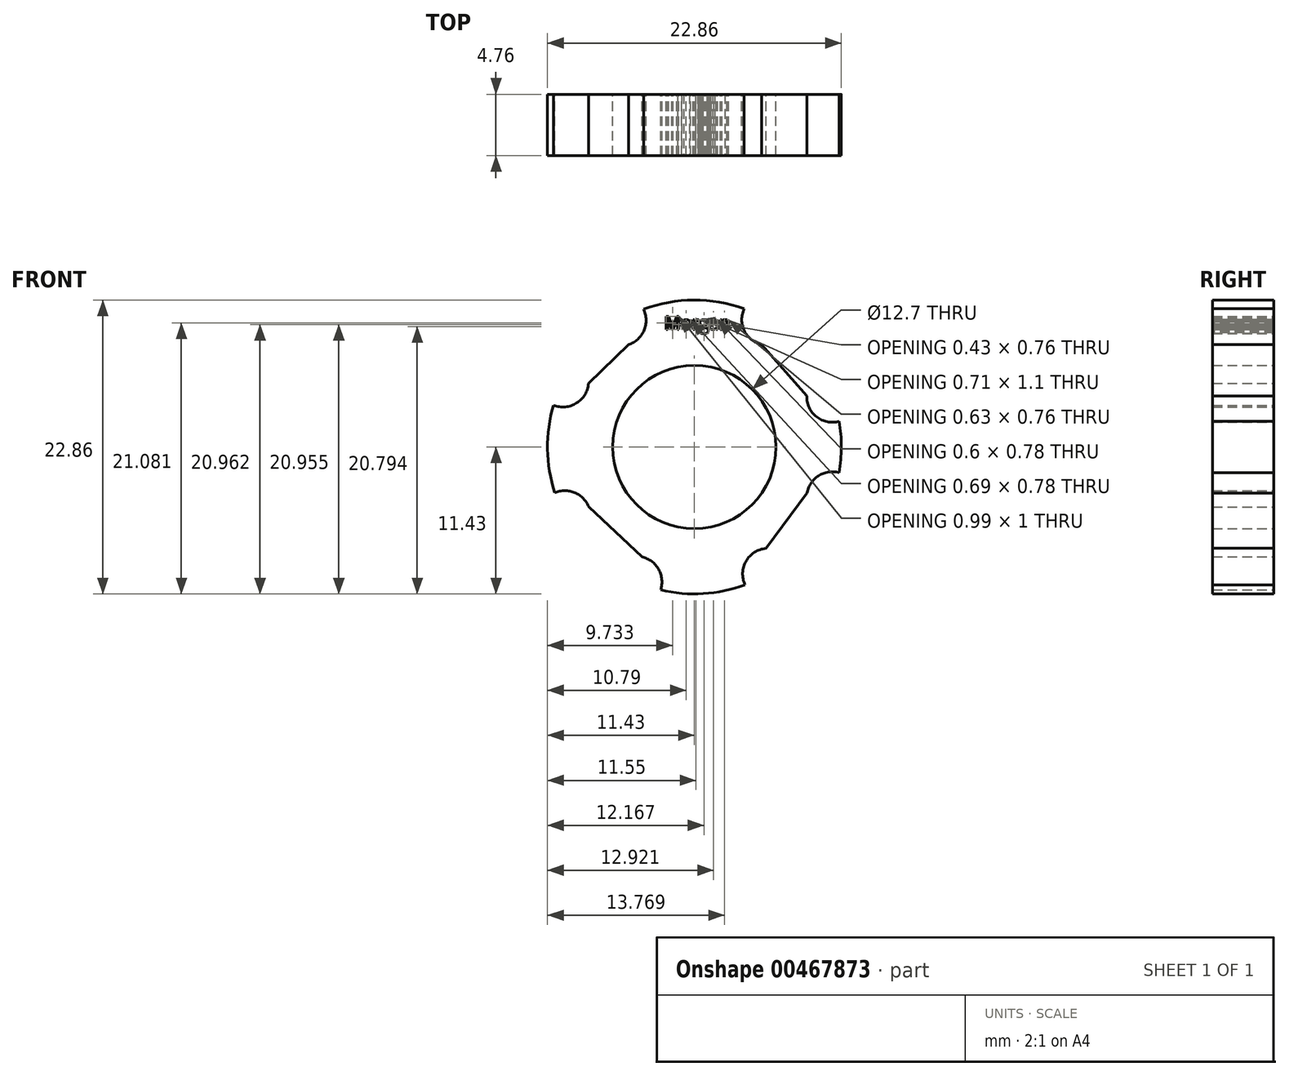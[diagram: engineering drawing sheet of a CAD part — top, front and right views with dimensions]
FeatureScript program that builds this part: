
annotation { "Feature Type Name" : "Feature", "Feature Type Description" : "" }
export const myFeature = defineFeature(function(context is Context, id is Id, definition is map)
    precondition{}
    {
        {
            var Q0;
            Q0=qCreatedBy(makeId("Front.planeOp"),FACE);
            var sketch = newSketch(context, id + "F0", { "sketchPlane" : qUnion([Q0])});
            skCircle(sketch, "E0", {"center": v(0, 0) * mm, "radius": 6.35 * mm});
            skCircle(sketch, "E1.0", {"center": v(0, 0) * mm, "radius": 11.43 * mm});
            skCircle(sketch, "E2", {"center": v(5.68, 9.92) * mm, "radius": 2 * mm});
            skCircle(sketch, "E3.2.1", {"center": v(5.75, -9.88) * mm, "radius": 2 * mm});
            skCircle(sketch, "E4.1.0", {"center": v(10.74, 3.92) * mm, "radius": 2 * mm});
            skCircle(sketch, "E4.2.0", {"center": v(10.74, -3.92) * mm, "radius": 2 * mm});
            skLineSegment(sketch, "E4.anchor1", {"start": v(0, 0) * mm, "end": v(5.68, 9.92) * mm, "construction": true});
            skLineSegment(sketch, "E4.anchor2", {"start": v(0, 0) * mm, "end": v(10.74, -3.92) * mm, "construction": true});
            skCircle(sketch, "E5.2.0", {"center": v(-10.08, -5.4) * mm, "radius": 2 * mm});
            skLineSegment(sketch, "E5.anchor2", {"start": v(0, 0) * mm, "end": v(-10.08, -5.4) * mm, "construction": true});
            skCircle(sketch, "E6.1.0", {"center": v(-4.52, -10.5) * mm, "radius": 2 * mm});
            skCircle(sketch, "E6.2.0", {"center": v(-10.23, 5.1) * mm, "radius": 2 * mm});
            skLineSegment(sketch, "E6.anchor2", {"start": v(0, 0) * mm, "end": v(-10.23, 5.1) * mm, "construction": true});
            skCircle(sketch, "E7.1.0", {"center": v(-5.75, 9.86) * mm, "radius": 2 * mm});
            skPoint(sketch, "E7.center", {"position": v(-0.1, 0.05) * mm});
            skLineSegment(sketch, "E7.anchor1", {"start": v(-0.1, 0.05) * mm, "end": v(-10.23, 5.1) * mm, "construction": true});
            skLineSegment(sketch, "E7.anchor2", {"start": v(-0.1, 0.05) * mm, "end": v(0.6, 11.35) * mm, "construction": true});
            skLineSegment(sketch, "E8", {"start": v(-8.24, 4.95) * mm, "end": v(-5.12, 7.96) * mm});
            skLineSegment(sketch, "E9", {"start": v(5.24, 7.97) * mm, "end": v(8.74, 3.96) * mm});
            skLineSegment(sketch, "E10", {"start": v(8.77, -3.59) * mm, "end": v(5.57, -7.9) * mm});
            skLineSegment(sketch, "E11", {"start": v(-4.07, -8.55) * mm, "end": v(-8.21, -4.68) * mm});
            skText(sketch, "E12", { "text": "Morgan", "fontName": "OpenSans-Regular.ttf"});
            const initialGuessF0  = {"E12": [-0.00233, 0.00915, 1, 0, 0.00101]};
            skSetInitialGuess(sketch, initialGuessF0);
            skSolve(sketch);
        }
        {
            var Q0;
            Q0=makeQuery(id+"F0.imprint","IMPRINT",FACE,{"disambiguationData":[TD([[makeQuery(id+"F0.imprint","IMPRINT",EDGE,{"derivedFrom":sQuery(id+"F0.wireOp",EDGE,"E0")}),-1.0]])]});
            extrude(context, id + "F1", {"entities" : qUnion([Q0]), "depth" : 4.76 * mm});
        }
        {
            var Q0;
            Q0 = qSketchRegion(id + "F0", true);
            extrude(context, id + "F2", {"entities" : qUnion([Q0]), "operationType" : NewBodyOperationType.REMOVE, "oppositeDirection" : true, "depth" : 25.4 * mm});
        }
    });
